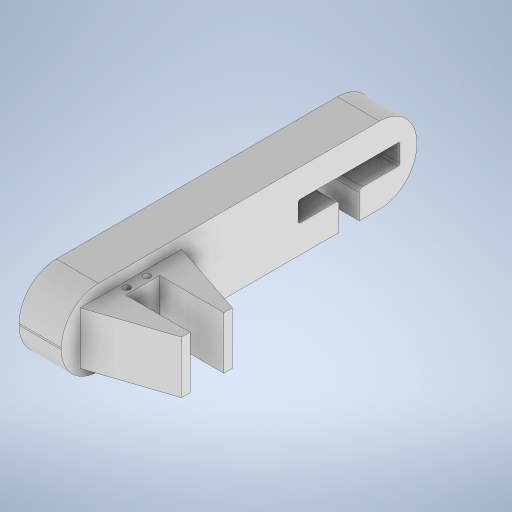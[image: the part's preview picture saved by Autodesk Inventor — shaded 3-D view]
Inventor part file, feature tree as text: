
AUTODESK INVENTOR PART (.ipt)
format: ipt  version: 2023 (Build 270158000, 158)  size: 310,272 bytes
history: native  units: mm
features: sketch x5, extrude x4, fillet x3, other x1
ambient origin geometry x8: Origin, YZ Plane, XZ Plane, XY Plane, X Axis, Y Axis, Z Axis, Center Point
bodies: Body1 (feature_tree)
feature tree (13):
  other  "實體1"
  extrude  "擠出1"  Depth=210.0mm
  fillet  "圓角1"  Radius=45.0mm
  extrude  "擠出2"  Depth=25.0mm TaperAngle=0.0deg
  fillet  "圓角2"  Radius=22.0mm
  fillet  "圓角3"  Radius=12.0mm
  extrude  "擠出3"  Depth=60.0mm
  extrude  "擠出4"  Depth=12.0mm
  sketch  "草圖5"
  sketch  "草圖1"
  sketch  "草圖2"
  sketch  "草圖3"
  sketch  "草圖4"
